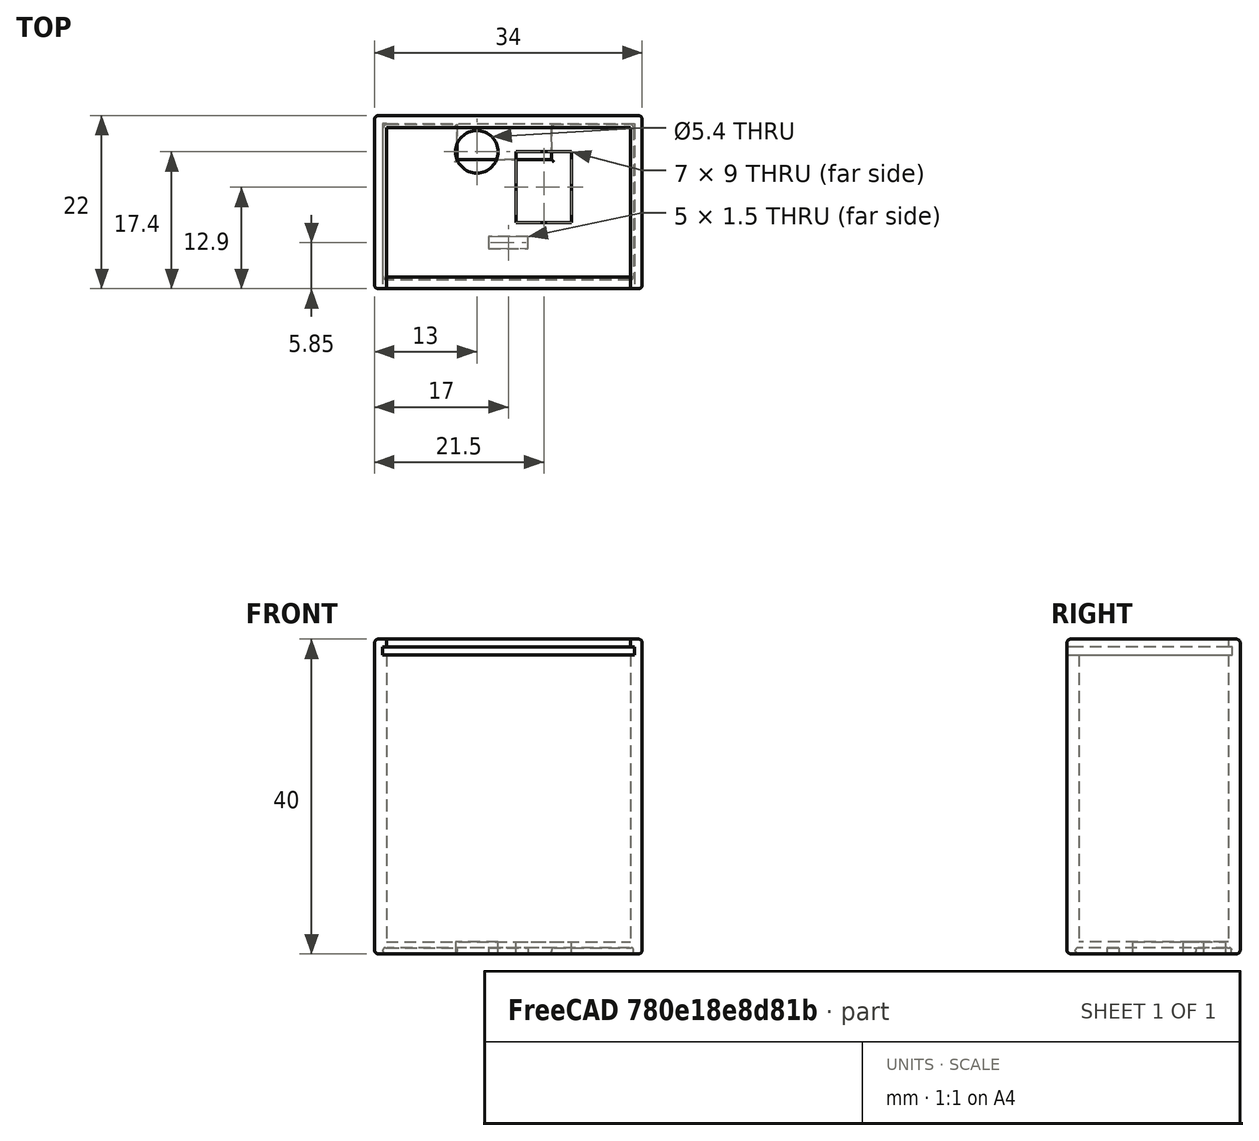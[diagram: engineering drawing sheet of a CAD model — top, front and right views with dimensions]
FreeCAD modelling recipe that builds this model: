
FCSTD DOCUMENT  (FreeCAD 0.18R4 (GitTag))
Label: IrDroid_Case
License: All rights reserved
LicenseURL: http://en.wikipedia.org/wiki/All_rights_reserved
objects: Sketcher::SketchObject×9, PartDesign::Pocket×7, PartDesign::Fillet×4, PartDesign::Pad×2, PartDesign::Body×2, Mesh::Feature×2, PartDesign::Mirrored×1
note: 34 computed .brp shape members not serialized (recipe doc carries the construction recipe); baked Part::Feature solids carry a one-line shape summary decoded from their .brp

FEATURE [Sketcher::SketchObject] Sketch
  MapMode = 5
  Support = -> [XY_Plane]
  sketch-geometry (4):
    g0: LineSegment StartX=-17 StartY=11 StartZ=0 EndX=17 EndY=11 EndZ=0
    g1: LineSegment StartX=17 StartY=11 StartZ=0 EndX=17 EndY=-11 EndZ=0
    g2: LineSegment StartX=17 StartY=-11 StartZ=0 EndX=-17 EndY=-11 EndZ=0
    g3: LineSegment StartX=-17 StartY=-11 StartZ=0 EndX=-17 EndY=11 EndZ=0
  constraints (11):
    c: Coincident(g0,g1)
    c: Coincident(g1,g2)
    c: Coincident(g2,g3)
    c: Coincident(g3,g0)
    c: Horizontal(g0)
    c: Horizontal(g2)
    c: Vertical(g1)
    c: Vertical(g3)
    c: DistanceX(g0,g0) = 34
    c: DistanceY(g1,g1) = 22
    c: Symmetric(g0,g2,g-1)
FEATURE [PartDesign::Pad] Pad
  Length = 40
  Length2 = 100
  Profile = -> Sketch
  Type = 0
FEATURE [Sketcher::SketchObject] Sketch001
  ExternalGeometry = -> [Pad]
  MapMode = 5
  Placement = pos=(0,0,40) rot=(0,0,1;0rad)
  Support = -> [Pad]
  sketch-geometry (4):
    g0: LineSegment StartX=-15.5 StartY=9.5 StartZ=0 EndX=15.5 EndY=9.5 EndZ=0
    g1: LineSegment StartX=15.5 StartY=9.5 StartZ=0 EndX=15.5 EndY=-9.5 EndZ=0
    g2: LineSegment StartX=15.5 StartY=-9.5 StartZ=0 EndX=-15.5 EndY=-9.5 EndZ=0
    g3: LineSegment StartX=-15.5 StartY=-9.5 StartZ=0 EndX=-15.5 EndY=9.5 EndZ=0
  constraints (12):
    c: Coincident(g0,g1)
    c: Coincident(g1,g2)
    c: Coincident(g2,g3)
    c: Coincident(g3,g0)
    c: Horizontal(g0)
    c: Horizontal(g2)
    c: Vertical(g1)
    c: Vertical(g3)
    c: DistanceX(g0,g0) = 31
    c: DistanceY(g1,g1) = 19
    c: DistanceX(g0,g-4) = 1.5
    c: DistanceY(g0,g-4) = 1.5
FEATURE [PartDesign::Pocket] Pocket
  BaseFeature = -> Pad
  Length = 38.5
  Length2 = 100
  Profile = -> Sketch001
  Type = 0
FEATURE [Sketcher::SketchObject] Sketch002
  ExternalGeometry = -> [Pocket]
  MapMode = 5
  Placement = pos=(0,0,0) rot=(1,0,0;3.14159rad)
  Support = -> [Pocket]
  sketch-geometry (5):
    g0: LineSegment StartX=8 StartY=-6.4 StartZ=0 EndX=1 EndY=-6.4 EndZ=0
    g1: LineSegment StartX=1 StartY=-6.4 StartZ=0 EndX=1 EndY=2.6 EndZ=0
    g2: LineSegment StartX=1 StartY=2.6 StartZ=0 EndX=8 EndY=2.6 EndZ=0
    g3: LineSegment StartX=8 StartY=2.6 StartZ=0 EndX=8 EndY=-6.4 EndZ=0
    g4: Circle CenterX=-4 CenterY=-6.4 CenterZ=0 NormalX=0 NormalY=0 NormalZ=1 AngleXU=0 Radius=2.7
  constraints (15):
    c: Coincident(g0,g1)
    c: Coincident(g1,g2)
    c: Coincident(g2,g3)
    c: Coincident(g3,g0)
    c: Horizontal(g0)
    c: Horizontal(g2)
    c: Vertical(g1)
    c: Vertical(g3)
    c: DistanceY(g3,g3) = 9
    c: DistanceX(g2,g2) = 7
    c: DistanceY(g0,g-4) = -4.6
    c: DistanceX(g0,g-4) = 16
    c: Radius(g4) = 2.7
    c: DistanceX(g4,g0) = 12
    c: DistanceY(g-4,g4) = 4.6
FEATURE [PartDesign::Pocket] Pocket001
  BaseFeature = -> Pocket
  Length = 5
  Length2 = 100
  Profile = -> Sketch002
  Type = 1
FEATURE [Sketcher::SketchObject] Sketch003
  ExternalGeometry = -> [Pocket001]
  MapMode = 5
  Placement = pos=(0,-11,0) rot=(1,0,0;1.5708rad)
  Support = -> [Pocket001]
  sketch-geometry (4):
    g0: LineSegment StartX=-15.5 StartY=40 StartZ=0 EndX=15.5 EndY=40 EndZ=0
    g1: LineSegment StartX=15.5 StartY=40 StartZ=0 EndX=15.5 EndY=38 EndZ=0
    g2: LineSegment StartX=15.5 StartY=38 StartZ=0 EndX=-15.5 EndY=38 EndZ=0
    g3: LineSegment StartX=-15.5 StartY=38 StartZ=0 EndX=-15.5 EndY=40 EndZ=0
  constraints (12):
    c: Coincident(g0,g1)
    c: Coincident(g1,g2)
    c: Coincident(g2,g3)
    c: Coincident(g3,g0)
    c: Horizontal(g0)
    c: Horizontal(g2)
    c: Vertical(g1)
    c: Vertical(g3)
    c: DistanceY(g1,g1) = 2
    c: DistanceY(g0,g-5) = 0
    c: DistanceX(g1,g-5) = 1.5
    c: DistanceX(g-4,g2) = 1.5
FEATURE [PartDesign::Pocket] Pocket002
  BaseFeature = -> Pocket001
  Length = 1.5
  Length2 = 100
  Profile = -> Sketch003
  Type = 0
FEATURE [Sketcher::SketchObject] Sketch004
  ExternalGeometry = -> [Pocket002]
  MapMode = 5
  Placement = pos=(15.5,0,0) rot=(0.57735,-0.57735,-0.57735;2.0944rad)
  Support = -> [Pocket002]
  sketch-geometry (4):
    g0: LineSegment StartX=-10 StartY=39 StartZ=0 EndX=11 EndY=39 EndZ=0
    g1: LineSegment StartX=11 StartY=39 StartZ=0 EndX=11 EndY=38 EndZ=0
    g2: LineSegment StartX=11 StartY=38 StartZ=0 EndX=-10 EndY=38 EndZ=0
    g3: LineSegment StartX=-10 StartY=38 StartZ=0 EndX=-10 EndY=39 EndZ=0
  constraints (12):
    c: Coincident(g0,g1)
    c: Coincident(g1,g2)
    c: Coincident(g2,g3)
    c: Coincident(g3,g0)
    c: Horizontal(g0)
    c: Horizontal(g2)
    c: Vertical(g1)
    c: Vertical(g3)
    c: DistanceY(g1,g1) = 1
    c: DistanceX(g-4,g0) = -0.5
    c: DistanceY(g-4,g0) = 37.5
    c: DistanceX(g0,g0) = 21
FEATURE [PartDesign::Pocket] Pocket003
  BaseFeature = -> Pocket002
  Length = 0.5
  Length2 = 100
  Profile = -> Sketch004
  Type = 0
FEATURE [PartDesign::Mirrored] Mirrored
  BaseFeature = -> Pocket003
  MirrorPlane = -> YZ_Plane
  Originals = -> [Pocket003]
FEATURE [Sketcher::SketchObject] Sketch006
  MapMode = 5
  Support = -> [XY_Plane001]
  sketch-geometry (4):
    g0: LineSegment StartX=-15.9 StartY=9.9 StartZ=0 EndX=15.9 EndY=9.9 EndZ=0
    g1: LineSegment StartX=15.9 StartY=9.9 StartZ=0 EndX=15.9 EndY=-9.9 EndZ=0
    g2: LineSegment StartX=15.9 StartY=-9.9 StartZ=0 EndX=-15.9 EndY=-9.9 EndZ=0
    g3: LineSegment StartX=-15.9 StartY=-9.9 StartZ=0 EndX=-15.9 EndY=9.9 EndZ=0
  constraints (11):
    c: Coincident(g0,g1)
    c: Coincident(g1,g2)
    c: Coincident(g2,g3)
    c: Coincident(g3,g0)
    c: Horizontal(g0)
    c: Horizontal(g2)
    c: Vertical(g1)
    c: Vertical(g3)
    c: DistanceX(g0,g0) = 31.8
    c: DistanceY(g1,g1) = 19.8
    c: Symmetric(g0,g2,g-1)
FEATURE [PartDesign::Pad] Pad001
  Length = 0.8
  Length2 = 100
  Profile = -> Sketch006
  Type = 0
FEATURE [Sketcher::SketchObject] Sketch007
  ExternalGeometry = -> [Pad001]
  MapMode = 5
  Placement = pos=(0,0,0.8) rot=(0,0,1;0rad)
  Support = -> [Pad001]
  sketch-geometry (4):
    g0: LineSegment StartX=-6.5 StartY=9.9 StartZ=0 EndX=5.5 EndY=9.9 EndZ=0
    g1: LineSegment StartX=5.5 StartY=9.9 StartZ=0 EndX=5.5 EndY=5.4 EndZ=0
    g2: LineSegment StartX=5.5 StartY=5.4 StartZ=0 EndX=-6.5 EndY=5.4 EndZ=0
    g3: LineSegment StartX=-6.5 StartY=5.4 StartZ=0 EndX=-6.5 EndY=9.9 EndZ=0
  constraints (12):
    c: Coincident(g0,g1)
    c: Coincident(g1,g2)
    c: Coincident(g2,g3)
    c: Coincident(g3,g0)
    c: Horizontal(g0)
    c: Horizontal(g2)
    c: Vertical(g1)
    c: Vertical(g3)
    c: DistanceY(g1,g1) = 4.5
    c: DistanceX(g2,g2) = 12
    c: DistanceX(g2,g-1) = 6.5
    c: DistanceY(g0,g-3) = 0
FEATURE [PartDesign::Pocket] Pocket005
  BaseFeature = -> Pad001
  Length = 5
  Length2 = 100
  Profile = -> Sketch007
  Type = 1
FEATURE [Sketcher::SketchObject] Sketch008
  ExternalGeometry = -> [Pocket005]
  MapMode = 5
  Placement = pos=(0,0,0.8) rot=(0,0,1;0rad)
  Support = -> [Pocket005]
  sketch-geometry (4):
    g0: LineSegment StartX=-2.5 StartY=-4.4 StartZ=0 EndX=2.5 EndY=-4.4 EndZ=0
    g1: LineSegment StartX=2.5 StartY=-4.4 StartZ=0 EndX=2.5 EndY=-5.9 EndZ=0
    g2: LineSegment StartX=2.5 StartY=-5.9 StartZ=0 EndX=-2.5 EndY=-5.9 EndZ=0
    g3: LineSegment StartX=-2.5 StartY=-5.9 StartZ=0 EndX=-2.5 EndY=-4.4 EndZ=0
  constraints (12):
    c: Coincident(g0,g1)
    c: Coincident(g1,g2)
    c: Coincident(g2,g3)
    c: Coincident(g3,g0)
    c: Horizontal(g0)
    c: Horizontal(g2)
    c: Vertical(g1)
    c: Vertical(g3)
    c: DistanceX(g0,g0) = 5
    c: DistanceY(g1,g1) = 1.5
    c: DistanceX(g2,g-1) = 2.5
    c: DistanceY(g-3,g1) = 4
FEATURE [PartDesign::Pocket] Pocket006
  BaseFeature = -> Pocket005
  Length = 5
  Length2 = 100
  Profile = -> Sketch008
  Type = 1
FEATURE [Sketcher::SketchObject] Sketch009
  ExternalGeometry = -> [Mirrored]
  MapMode = 5
  Placement = pos=(0,9.5,0) rot=(1,0,0;1.5708rad)
  Support = -> [Mirrored]
  sketch-geometry (4):
    g0: LineSegment StartX=-16 StartY=39 StartZ=0 EndX=16 EndY=39 EndZ=0
    g1: LineSegment StartX=16 StartY=39 StartZ=0 EndX=16 EndY=38 EndZ=0
    g2: LineSegment StartX=16 StartY=38 StartZ=0 EndX=-16 EndY=38 EndZ=0
    g3: LineSegment StartX=-16 StartY=38 StartZ=0 EndX=-16 EndY=39 EndZ=0
  constraints (12):
    c: Coincident(g0,g1)
    c: Coincident(g1,g2)
    c: Coincident(g2,g3)
    c: Coincident(g3,g0)
    c: Horizontal(g0)
    c: Horizontal(g2)
    c: Vertical(g1)
    c: Vertical(g3)
    c: DistanceY(g1,g1) = 1
    c: DistanceX(g-3,g0) = -0.5
    c: DistanceX(g0,g0) = 32
    c: DistanceY(g-1,g0) = 39
FEATURE [PartDesign::Pocket] Pocket007
  BaseFeature = -> Mirrored
  Length = 0.5
  Length2 = 100
  Profile = -> Sketch009
  Type = 0
FEATURE [PartDesign::Fillet] Fillet
  Base = -> Pocket007 [Edge8,Edge9,Edge2,Edge3,Edge1,Edge6,Edge5,Edge11]
  BaseFeature = -> Pocket007
  Radius = 0.5
FEATURE [PartDesign::Fillet] Fillet001
  Base = -> Fillet [Edge12,Edge1,Edge5]
  BaseFeature = -> Fillet
  Radius = 0.5
FEATURE [PartDesign::Body] Body  label="Case"
  Group = -> [Sketch,Pad,Sketch001,Pocket,Sketch002,Pocket001,Sketch003,Pocket002,Sketch004,Pocket003,Mirrored,Sketch009,Pocket007,Fillet,Fillet001]
  Origin = -> Origin
  Tip = -> Fillet001
FEATURE [PartDesign::Fillet] Fillet002
  Base = -> Pocket006 [Edge29,Edge30,Edge4,Edge28]
  BaseFeature = -> Pocket006
  Radius = 0.5
FEATURE [PartDesign::Fillet] Fillet003
  Base = -> Fillet002 [Edge24,Edge5,Edge1,Edge4,Edge29,Edge12,Edge14,Edge31,Edge22,Edge15,Edge32,Edge28,Edge11,Edge10]
  BaseFeature = -> Fillet002
  Radius = 0.3
FEATURE [PartDesign::Body] Body001  label="Top"
  Group = -> [Sketch006,Pad001,Sketch007,Pocket005,Sketch008,Pocket006,Fillet002,Fillet003]
  Origin = -> Origin001
  Tip = -> Fillet003
FEATURE [Mesh::Feature] Mesh  label="RcDroidTop_V1"
FEATURE [Mesh::Feature] Mesh001  label="RcDroidCase_V1"
